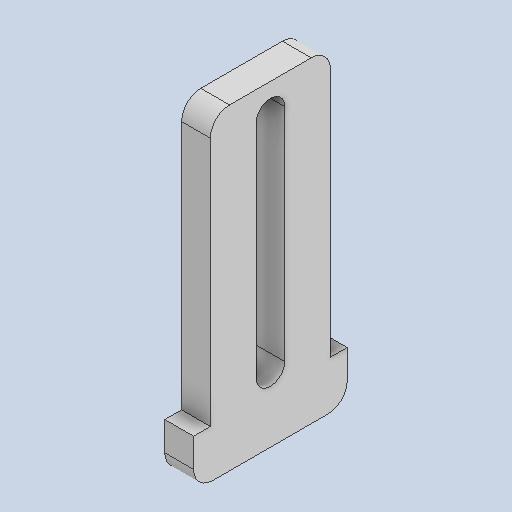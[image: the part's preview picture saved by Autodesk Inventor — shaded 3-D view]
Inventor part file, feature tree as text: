
AUTODESK INVENTOR PART (.ipt)
format: ipt  version: 2023 (Build 270158000, 158)  size: 111,104 bytes
history: native  units: in
note: dims shown in document units (in); Inventor stores cm internally (conversion verified against a paired STEP export)
features: other x3, sketch x1
ambient origin geometry x8: Origin, YZ Plane, XZ Plane, XY Plane, X Axis, Y Axis, Z Axis, Center Point
bodies: Body1 (feature_tree)
feature tree (4):
  other  "Ga motor 1.ipt"
  other  "Solid3::Ga motor 1.ipt"
  other  "TaggingFeature1"
  sketch  "Sketch1"  dims[d0=0.3937in]
